# Revit family: 再々39_LS715 + TLE26SM1A + TLDP2107J(壁給水)(壁排水)
name_source: partatom
category: 衛生器具
units: mm (PartAtom-declared; Revit-internal decimal feet)

## family parameters
OmniClass タイトル = Sanitary, Laundry, and Cleaning Equipment
OmniClass 番号 = 23.45.00.00
パーツ タイプ = 標準
ロード時にボイドで切り取り = はい
丸型コネクタ寸法 = 直径を使用
作業面ベース = いいえ
共有 = いいえ
常に垂直 = はい
部屋計算ポイント = いいえ

## types (2) — shared parameters
3Dファイル形式 = rfa
BLCJ仕様バージョン = Version1.0
URL = https://jp.toto.com
カウンター色 = TOTO カウンター
キーノート = 0表示の場合は商品仕様と設計数量をご確認ください
データ作成ソフトVer = Revit ver.2019
モデル = LS715 + TLE26SM1A + TLDP2107J
付属単位 = TLE26SM1A + TLDP2107J
企業コード = 504860
使用水 = 上水
周波数 = 0 Hz
商品情報URL = https://www.com-et.com
商品紹介URL = https://jp.toto.com
奥行 = 600
幅 = 900
排気配管 = いいえ
排水接続口 = 32
排水配管 = はい
最低使用圧力 = 0.1 MPa
最高使用圧力 = 0.8 MPa
極数 = 2
構成品番 = LS715 + TLE26SM1A + TLDP2107J
水配管 = はい
洗浄水量 = 0.0 L
流量（L/min） = 2
消費電力 = 927 W
温水配管 = いいえ
相 = 1
給水接続口 = R1/2
給水接続口情報 = 15A
製品リリース年月 = 2022年8月
製品出荷対象 = 国内
製造元 = TOTO株式会社
説明 = ベッセル式洗面器
負荷分類 = 9_コンセント
陶器色 = TOTO_陶器・便座♯NW1
電圧 = 100 V
zero-valued in all types: 上水負荷単位, 中水負荷単位, 排水芯・排水高さ, 標準取付高さ, 汚水負荷単位, 給水負荷単位(水栓), 給水負荷単位(洗浄), 給湯負荷単位, 雑排水負荷単位

## per-type parameters (varying)
| type | あふれ面高さ |
| あふれ面高さ(750mm) | 750  [stored 2.46063 ft] |
| あふれ面高さ(800mm) | 800  [stored 2.62467 ft] |

note: [stored X ft] marks values corroborated as IEEE doubles in the binary element streams (Revit-internal decimal feet)
